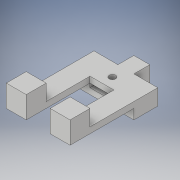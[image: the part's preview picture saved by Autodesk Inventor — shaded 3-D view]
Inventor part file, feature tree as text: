
AUTODESK INVENTOR PART (.ipt)
format: ipt  version: 2018 (Build 220112000, 112)  size: 165,376 bytes
history: native  units: in
note: dims shown in document units (in); Inventor stores cm internally (conversion verified against a paired STEP export)
features: extrude x6, sketch x6
ambient origin geometry x8: Origin, YZ Plane, XZ Plane, XY Plane, X Axis, Y Axis, Z Axis, Center Point
bodies: Solid1 (feature_tree)
feature tree (12):
  extrude  "Extrusion1"  Depth=0.5in
  extrude  "Extrusion2"  Depth=0.5in TaperAngle=0.0deg
  extrude  "Extrusion3"  Depth=1.25in
  extrude  "Extrusion4"  Depth=0.375in
  extrude  "Extrusion5"  Depth=0.1in TaperAngle=0.0deg
  extrude  "Extrusion6"  Depth=0.5in
  sketch  "Sketch1"  dims[d0=0.5in d1=0.5in]
  sketch  "Sketch2"  dims[d2=0.375in d3=0.5in d4=0.0in]
  sketch  "Sketch3"  dims[d5=0.75in d6=1.25in]
  sketch  "Sketch4"  dims[d9=0.375in d10=0.375in]
  sketch  "Sketch5"  dims[d11=0.75in d12=0.0in d13=0.1in d14=0.0in]
  sketch  "Sketch6"  dims[d15=0.328in d16=0.2031in d17=0.7875in d18=0.0in d19=2.0in d20=0.0in d21=0.625in d22=0.625in d23=0.5in d24=0.0in]
